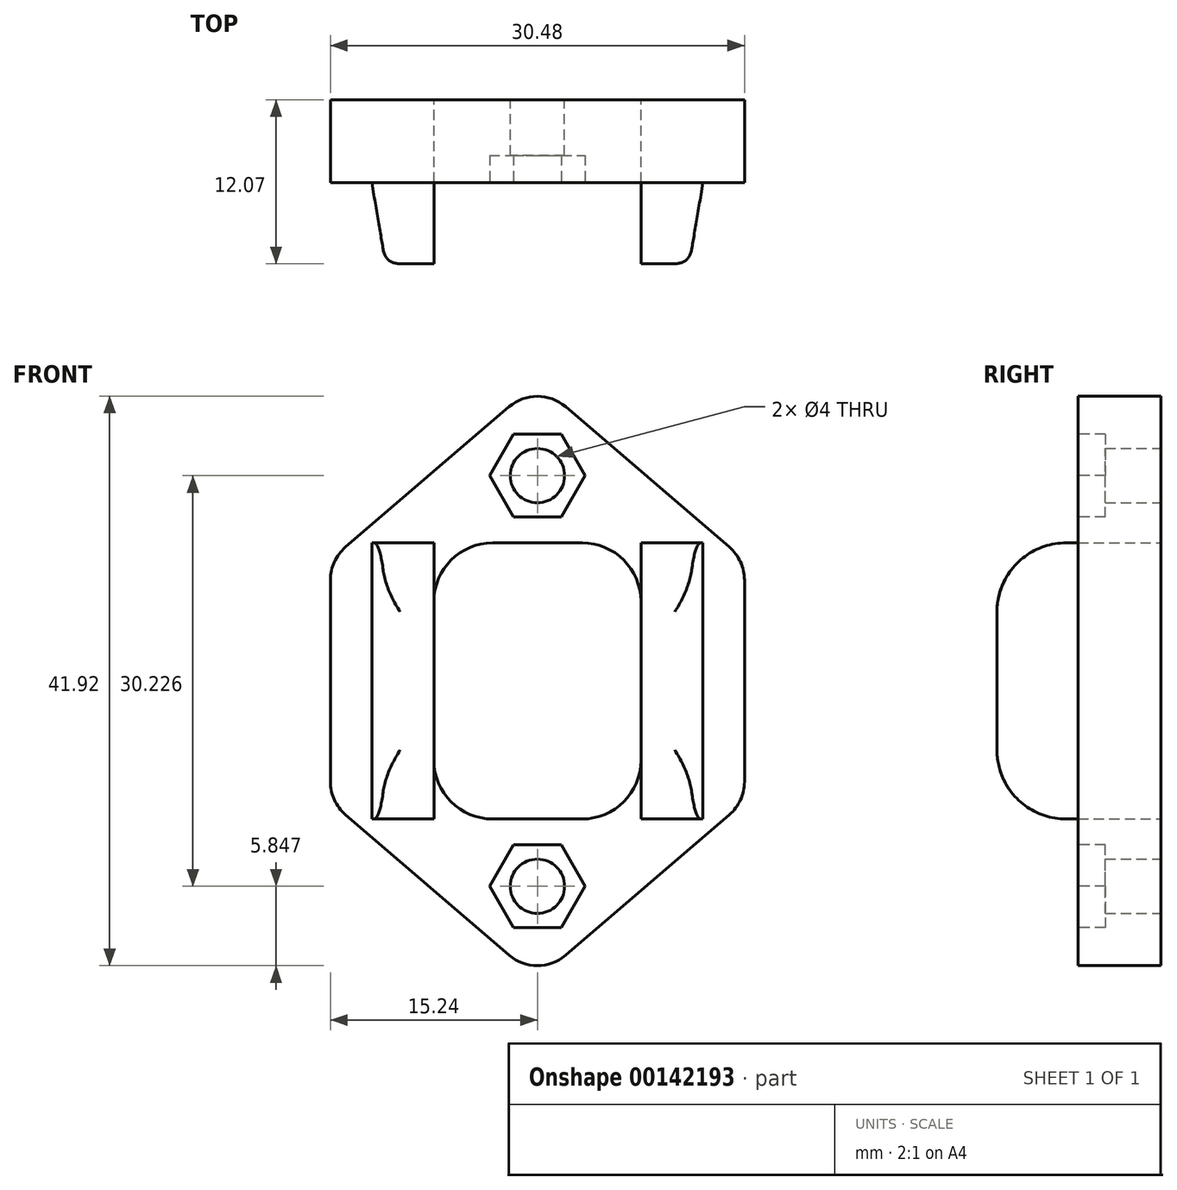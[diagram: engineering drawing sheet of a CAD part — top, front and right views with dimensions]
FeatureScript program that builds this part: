
annotation { "Feature Type Name" : "Feature", "Feature Type Description" : "" }
export const myFeature = defineFeature(function(context is Context, id is Id, definition is map)
    precondition{}
    {
        {
            var Q0;
            Q0=qCreatedBy(makeId("Front.planeOp"),FACE);
            var sketch = newSketch(context, id + "F0", { "sketchPlane" : qUnion([Q0])});
            skLineSegment(sketch, "E0.bottom", {"start": v(15.24, 20.96) * mm, "end": v(-15.24, 20.96) * mm, "construction": true});
            skLineSegment(sketch, "E0.top", {"start": v(15.24, -20.96) * mm, "end": v(-15.24, -20.96) * mm, "construction": true});
            skLineSegment(sketch, "E0.left", {"start": v(15.24, 20.96) * mm, "end": v(15.24, -20.96) * mm, "construction": true});
            skLineSegment(sketch, "E0.right", {"start": v(-15.24, 20.96) * mm, "end": v(-15.24, -20.96) * mm, "construction": true});
            skPoint(sketch, "E0.middle", {"position": v(0, 0) * mm});
            skLineSegment(sketch, "E1", {"start": v(-15.24, 8.89) * mm, "end": v(15.24, 8.9) * mm, "construction": true});
            skArc(sketch, "E2", {"start": v(2.07, 20.19) * mm, "mid": v(0, 20.96) * mm, "end": v(-2.07, 20.19) * mm});
            skArc(sketch, "E3", {"start": v(-2.07, -20.19) * mm, "mid": v(0, -20.96) * mm, "end": v(2.07, -20.19) * mm});
            skLineSegment(sketch, "E4.MirrorCS", {"start": v(-15.24, -8.89) * mm, "end": v(15.24, -8.9) * mm, "construction": true});
            skLineSegment(sketch, "E5", {"start": v(-14.13, 9.84) * mm, "end": v(-2.07, 20.19) * mm});
            skLineSegment(sketch, "E6", {"start": v(14.13, 9.84) * mm, "end": v(2.07, 20.19) * mm});
            skLineSegment(sketch, "E7", {"start": v(-14.13, -9.84) * mm, "end": v(-2.07, -20.19) * mm});
            skLineSegment(sketch, "E8", {"start": v(14.13, -9.84) * mm, "end": v(2.07, -20.19) * mm});
            skLineSegment(sketch, "E9", {"start": v(-15.24, 7.43) * mm, "end": v(-15.24, -7.43) * mm});
            skLineSegment(sketch, "E10", {"start": v(15.24, 7.43) * mm, "end": v(15.24, -7.43) * mm});
            skPoint(sketch, "E11.visualSharp", {"position": v(-15.24, 8.89) * mm});
            skArc(sketch, "E11.filletArc", {"start": v(-14.13, 9.84) * mm, "mid": v(-14.95, 8.76) * mm, "end": v(-15.24, 7.43) * mm});
            skPoint(sketch, "E12.visualSharp", {"position": v(15.24, 8.9) * mm});
            skArc(sketch, "E12.filletArc", {"start": v(15.24, 7.43) * mm, "mid": v(14.95, 8.76) * mm, "end": v(14.13, 9.84) * mm});
            skPoint(sketch, "E13.visualSharp", {"position": v(15.24, -8.9) * mm});
            skArc(sketch, "E13.filletArc", {"start": v(14.13, -9.84) * mm, "mid": v(14.95, -8.76) * mm, "end": v(15.24, -7.43) * mm});
            skPoint(sketch, "E14.visualSharp", {"position": v(-15.24, -8.89) * mm});
            skArc(sketch, "E14.filletArc", {"start": v(-15.24, -7.43) * mm, "mid": v(-14.95, -8.76) * mm, "end": v(-14.13, -9.84) * mm});
            skLineSegment(sketch, "E15", {"start": v(-15.24, 15.11) * mm, "end": v(15.24, 15.11) * mm, "construction": true});
            skLineSegment(sketch, "E16.MirrorCS", {"start": v(-15.24, -15.11) * mm, "end": v(15.24, -15.11) * mm, "construction": true});
            skCircle(sketch, "E17", {"center": v(0, 15.11) * mm, "radius": 2 * mm});
            skCircle(sketch, "E18", {"center": v(0, -15.11) * mm, "radius": 2 * mm});
            skSolve(sketch);
        }
        {
            var Q0;
            Q0=makeQuery(id+"F0.imprint","IMPRINT",FACE,{"disambiguationData":[TD([[makeQuery(id+"F0.imprint","IMPRINT",EDGE,{"derivedFrom":sQuery(id+"F0.wireOp",EDGE,"E2")}),1.0]])]});
            extrude(context, id + "F1", {"entities" : qUnion([Q0]), "depth" : 6.1 * mm});
        }
        {
            var Q0;
            Q0=qCreatedBy(makeId("Front.planeOp"),FACE);
            var sketch = newSketch(context, id + "F2", { "sketchPlane" : qUnion([Q0])});
            skLineSegment(sketch, "E19.bottom", {"start": v(15.24, 20.95) * mm, "end": v(-15.24, 20.95) * mm, "construction": true});
            skLineSegment(sketch, "E19.top", {"start": v(15.24, -20.96) * mm, "end": v(-15.24, -20.96) * mm, "construction": true});
            skLineSegment(sketch, "E19.left", {"start": v(15.24, 20.95) * mm, "end": v(15.24, -20.96) * mm, "construction": true});
            skLineSegment(sketch, "E19.right", {"start": v(-15.24, 20.95) * mm, "end": v(-15.24, -20.96) * mm, "construction": true});
            skPoint(sketch, "E19.middle", {"position": v(0, 0) * mm});
            skLineSegment(sketch, "E20", {"start": v(-15.24, 10.16) * mm, "end": v(15.24, 10.16) * mm, "construction": true});
            skLineSegment(sketch, "E21.MirrorCS", {"start": v(-15.24, -10.16) * mm, "end": v(15.24, -10.16) * mm, "construction": true});
            skPoint(sketch, "E22.visualSharp", {"position": v(-15.24, 10.16) * mm});
            skPoint(sketch, "E23.visualSharp", {"position": v(15.24, 10.16) * mm});
            skPoint(sketch, "E24.visualSharp", {"position": v(15.24, -10.16) * mm});
            skPoint(sketch, "E25.visualSharp", {"position": v(-15.24, -10.16) * mm});
            skLineSegment(sketch, "E26", {"start": v(-15.24, 15.11) * mm, "end": v(15.24, 15.11) * mm, "construction": true});
            skLineSegment(sketch, "E27.MirrorCS", {"start": v(-15.24, -15.11) * mm, "end": v(15.24, -15.11) * mm, "construction": true});
            skLineSegment(sketch, "E28", {"start": v(-7.62, -20.96) * mm, "end": v(-7.62, 20.95) * mm, "construction": true});
            skLineSegment(sketch, "E29.bottom", {"start": v(-7.62, 10.16) * mm, "end": v(7.62, 10.16) * mm});
            skLineSegment(sketch, "E29.top", {"start": v(-7.62, -10.16) * mm, "end": v(7.62, -10.16) * mm});
            skLineSegment(sketch, "E29.left", {"start": v(-7.62, 10.16) * mm, "end": v(-7.62, -10.16) * mm});
            skLineSegment(sketch, "E29.right", {"start": v(7.62, 10.16) * mm, "end": v(7.62, -10.16) * mm});
            skPoint(sketch, "E30.visualSharp", {"position": v(7.62, 10.16) * mm});
            skPoint(sketch, "E31.visualSharp", {"position": v(-7.62, 10.16) * mm});
            skPoint(sketch, "E32.visualSharp", {"position": v(-7.62, -10.16) * mm});
            skPoint(sketch, "E33.visualSharp", {"position": v(7.62, -10.16) * mm});
            skSolve(sketch);
        }
        {
            var Q0;
            Q0 = qSketchRegion(id + "F2", true);
            extrude(context, id + "F3", {"entities" : qUnion([Q0]), "operationType" : NewBodyOperationType.REMOVE, "depth" : 25.4 * mm});
        }
        {
            var Q0;
            Q0=makeQuery(id+"F1.opExtrude","CAP_FACE",FACE,{"disambiguationData":[OSD([sQuery(id+"F0.wireOp",EDGE,"E2"),sQuery(id+"F0.wireOp",EDGE,"E3"),sQuery(id+"F0.wireOp",EDGE,"E5"),sQuery(id+"F0.wireOp",EDGE,"E6"),sQuery(id+"F0.wireOp",EDGE,"E7"),sQuery(id+"F0.wireOp",EDGE,"E8"),sQuery(id+"F0.wireOp",EDGE,"E9"),sQuery(id+"F0.wireOp",EDGE,"E10"),sQuery(id+"F0.wireOp",EDGE,"E11.filletArc"),sQuery(id+"F0.wireOp",EDGE,"E12.filletArc"),sQuery(id+"F0.wireOp",EDGE,"E13.filletArc"),sQuery(id+"F0.wireOp",EDGE,"E14.filletArc"),sQuery(id+"F0.wireOp",EDGE,"E17"),sQuery(id+"F0.wireOp",EDGE,"E18")])],"isStart":false});
            var sketch = newSketch(context, id + "F4", { "sketchPlane" : qUnion([Q0])});
            skLineSegment(sketch, "E34", {"start": v(-12.53, 15.11) * mm, "end": v(12.12, 15.11) * mm, "construction": true});
            skCircle(sketch, "E35.cCircle", {"center": v(0, 15.11) * mm, "radius": 3.05 * mm, "construction": true});
            skLineSegment(sketch, "E35.0", {"start": v(1.76, 18.16) * mm, "end": v(3.52, 15.11) * mm});
            skLineSegment(sketch, "E35.1", {"start": v(3.52, 15.11) * mm, "end": v(1.76, 12.06) * mm});
            skLineSegment(sketch, "E35.2", {"start": v(1.76, 12.06) * mm, "end": v(-1.76, 12.07) * mm});
            skLineSegment(sketch, "E35.3", {"start": v(-1.76, 12.07) * mm, "end": v(-3.52, 15.11) * mm});
            skLineSegment(sketch, "E35.4", {"start": v(-3.52, 15.11) * mm, "end": v(-1.76, 18.16) * mm});
            skLineSegment(sketch, "E35.5", {"start": v(-1.76, 18.16) * mm, "end": v(1.76, 18.16) * mm});
            skPoint(sketch, "E35.0.midPoint", {"position": v(2.64, 16.64) * mm});
            skLineSegment(sketch, "E36.MirrorCS", {"start": v(-1.76, -18.16) * mm, "end": v(1.76, -18.16) * mm});
            skLineSegment(sketch, "E37.MirrorCS", {"start": v(-3.52, -15.11) * mm, "end": v(-1.76, -18.16) * mm});
            skLineSegment(sketch, "E38.MirrorCS", {"start": v(-1.76, -12.07) * mm, "end": v(-3.52, -15.11) * mm});
            skLineSegment(sketch, "E39.MirrorCS", {"start": v(1.76, -12.06) * mm, "end": v(-1.76, -12.07) * mm});
            skLineSegment(sketch, "E40.MirrorCS", {"start": v(3.52, -15.11) * mm, "end": v(1.76, -12.06) * mm});
            skLineSegment(sketch, "E41.MirrorCS", {"start": v(1.76, -18.16) * mm, "end": v(3.52, -15.11) * mm});
            skCircle(sketch, "E42.MirrorC", {"center": v(0, -15.11) * mm, "radius": 3.05 * mm, "construction": true});
            skPoint(sketch, "E43.MirrorP", {"position": v(2.64, -16.64) * mm});
            skSolve(sketch);
        }
        {
            var Q0;
            Q0 = qSketchRegion(id + "F4", true);
            extrude(context, id + "F5", {"entities" : qUnion([Q0]), "operationType" : NewBodyOperationType.REMOVE, "oppositeDirection" : true, "depth" : 2 * mm});
        }
        {
            var Q0;
            Q0=makeQuery(id+"F3.boolean.opBoolean","COPY",FACE,{"derivedFrom":makeQuery(id+"F3.opExtrude","SWEPT_FACE",FACE,{"disambiguationData":[OSD([sQuery(id+"F2.wireOp",EDGE,"E29.top")])]})});
            var sketch = newSketch(context, id + "F6", { "sketchPlane" : qUnion([Q0])});
            skLineSegment(sketch, "E44.top", {"start": v(-7.62, -12.07) * mm, "end": v(-11.18, -12.07) * mm});
            skLineSegment(sketch, "E44.left", {"start": v(-7.62, -6.1) * mm, "end": v(-7.62, -12.07) * mm});
            skLineSegment(sketch, "E45", {"start": v(-11.18, -12.07) * mm, "end": v(-12.19, -6.1) * mm});
            skLineSegment(sketch, "E46", {"start": v(-12.19, -6.1) * mm, "end": v(-7.62, -6.1) * mm});
            skLineSegment(sketch, "E47.MirrorCS", {"start": v(7.62, -12.07) * mm, "end": v(11.18, -12.07) * mm});
            skLineSegment(sketch, "E48.MirrorCS", {"start": v(12.19, -6.1) * mm, "end": v(7.62, -6.1) * mm});
            skLineSegment(sketch, "E49.MirrorCS", {"start": v(11.18, -12.07) * mm, "end": v(12.19, -6.1) * mm});
            skLineSegment(sketch, "E50.MirrorCS", {"start": v(7.62, -6.1) * mm, "end": v(7.62, -12.07) * mm});
            skSolve(sketch);
        }
        {
            var Q0;
            Q0 = qSketchRegion(id + "F6", true);
            var Q1;
            Q1=makeQuery(id+"F3.boolean.opBoolean","COPY",FACE,{"derivedFrom":makeQuery(id+"F3.opExtrude","SWEPT_FACE",FACE,{"disambiguationData":[OSD([sQuery(id+"F2.wireOp",EDGE,"E29.bottom")])]})});
            extrude(context, id + "F7", {"entities" : qUnion([Q0]), "operationType" : NewBodyOperationType.ADD, "endBoundEntityFace" : qUnion([Q1]), "depth" : 20.32 * mm});
        }
        {
            var Q0;
            Q0=makeQuery(id+"F7.opExtrude","SWEPT_EDGE",EDGE,{"disambiguationData":[OSD([sQuery(id+"F6.wireOp",EDGE,"E45"),sQuery(id+"F6.wireOp",EDGE,"E46")])]});
            var Q1;
            Q1=makeQuery(id+"F7.opExtrude","CAP_EDGE",EDGE,{"disambiguationData":[OSD([sQuery(id+"F6.wireOp",EDGE,"E46")])],"isStart":false});
            var Q2;
            Q2=makeQuery(id+"F7.opExtrude","CAP_EDGE",EDGE,{"disambiguationData":[OSD([sQuery(id+"F6.wireOp",EDGE,"E46")])],"isStart":true});
            var Q3;
            Q3=makeQuery(id+"F7.opExtrude","CAP_EDGE",EDGE,{"disambiguationData":[OSD([sQuery(id+"F6.wireOp",EDGE,"E48.MirrorCS")])],"isStart":true});
            var Q4;
            Q4=makeQuery(id+"F7.opExtrude","SWEPT_EDGE",EDGE,{"disambiguationData":[OSD([sQuery(id+"F6.wireOp",EDGE,"E48.MirrorCS"),sQuery(id+"F6.wireOp",EDGE,"E49.MirrorCS")])]});
            var Q5;
            Q5=makeQuery(id+"F7.opExtrude","CAP_EDGE",EDGE,{"disambiguationData":[OSD([sQuery(id+"F6.wireOp",EDGE,"E48.MirrorCS")])],"isStart":false});
            var Q6;
            Q6=makeQuery(id+"F7.opExtrude","SWEPT_EDGE",EDGE,{"disambiguationData":[OSD([sQuery(id+"F6.wireOp",EDGE,"E47.MirrorCS"),sQuery(id+"F6.wireOp",EDGE,"E49.MirrorCS")])]});
            var Q7;
            Q7=makeQuery(id+"F7.opExtrude","SWEPT_EDGE",EDGE,{"disambiguationData":[OSD([sQuery(id+"F6.wireOp",EDGE,"E44.top"),sQuery(id+"F6.wireOp",EDGE,"E45")])]});
            fillet(context, id + "F8", {"entities" : qUnion([Q0, Q1, Q2, Q3, Q4, Q5, Q6, Q7]), "radius" : 1.27 * mm, "tangentPropagation" : true, "rho" : 0.5, "crossSection" : FilletCrossSection.CONIC, "allowEdgeOverflow" : false});
        }
        {
            var Q0;
            Q0=makeQuery(id+"F7.opExtrude","CAP_EDGE",EDGE,{"disambiguationData":[OSD([sQuery(id+"F6.wireOp",EDGE,"E44.top")])],"isStart":false});
            var Q1;
            Q1=makeQuery(id+"F7.opExtrude","CAP_EDGE",EDGE,{"disambiguationData":[OSD([sQuery(id+"F6.wireOp",EDGE,"E44.top")])],"isStart":true});
            var Q2;
            Q2=makeQuery(id+"F7.opExtrude","CAP_EDGE",EDGE,{"disambiguationData":[OSD([sQuery(id+"F6.wireOp",EDGE,"E47.MirrorCS")])],"isStart":true});
            var Q3;
            Q3=makeQuery(id+"F7.opExtrude","CAP_EDGE",EDGE,{"disambiguationData":[OSD([sQuery(id+"F6.wireOp",EDGE,"E47.MirrorCS")])],"isStart":false});
            fillet(context, id + "F9", {"entities" : qUnion([Q0, Q1, Q2, Q3]), "radius" : 5.08 * mm, "allowEdgeOverflow" : false});
        }
        {
            var Q0;
            Q0=makeQuery(id+"F3.boolean.opBoolean","COPY",EDGE,{"derivedFrom":makeQuery(id+"F3.opExtrude","SWEPT_EDGE",EDGE,{"disambiguationData":[OSD([sQuery(id+"F2.wireOp",EDGE,"E29.bottom"),sQuery(id+"F2.wireOp",EDGE,"E29.left")])]})});
            var Q1;
            Q1=makeQuery(id+"F3.boolean.opBoolean","COPY",EDGE,{"derivedFrom":makeQuery(id+"F3.opExtrude","SWEPT_EDGE",EDGE,{"disambiguationData":[OSD([sQuery(id+"F2.wireOp",EDGE,"E29.bottom"),sQuery(id+"F2.wireOp",EDGE,"E29.right")])]})});
            var Q2;
            Q2=makeQuery(id+"F3.boolean.opBoolean","COPY",EDGE,{"derivedFrom":makeQuery(id+"F3.opExtrude","SWEPT_EDGE",EDGE,{"disambiguationData":[OSD([sQuery(id+"F2.wireOp",EDGE,"E29.top"),sQuery(id+"F2.wireOp",EDGE,"E29.right")])]})});
            var Q3;
            Q3=makeQuery(id+"F3.boolean.opBoolean","COPY",EDGE,{"derivedFrom":makeQuery(id+"F3.opExtrude","SWEPT_EDGE",EDGE,{"disambiguationData":[OSD([sQuery(id+"F2.wireOp",EDGE,"E29.top"),sQuery(id+"F2.wireOp",EDGE,"E29.left")])]})});
            fillet(context, id + "F10", {"entities" : qUnion([Q0, Q1, Q2, Q3]), "radius" : 4.32 * mm, "tangentPropagation" : true, "allowEdgeOverflow" : false});
        }
    });
